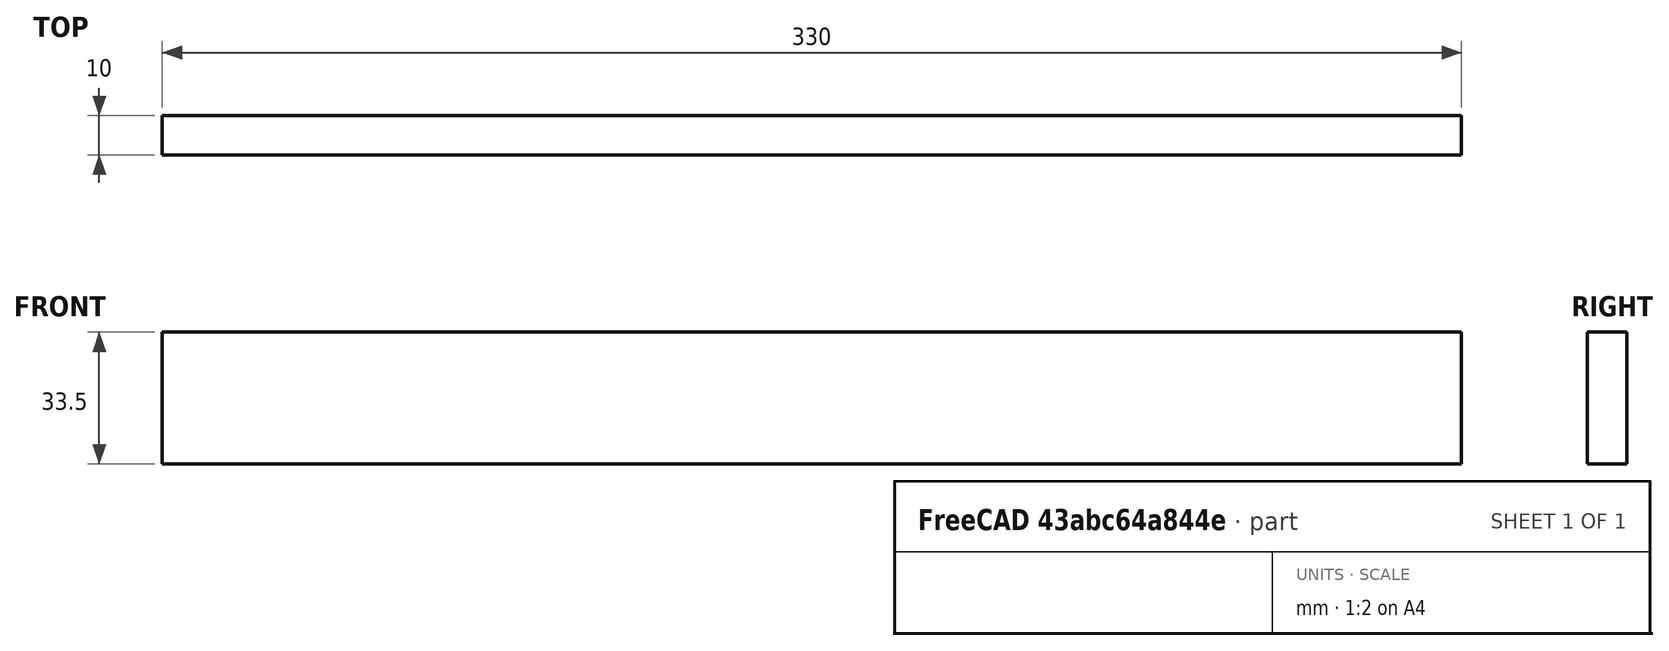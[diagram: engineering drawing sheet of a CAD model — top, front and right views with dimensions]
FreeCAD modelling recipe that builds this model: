
FCSTD DOCUMENT  (FreeCAD 0.18R16110 (Git))
Label: guide_330
License: All rights reserved
LicenseURL: http://en.wikipedia.org/wiki/All_rights_reserved
objects: App::Part×1, Sketcher::SketchObject×1, PartDesign::Pad×1, PartDesign::Body×1
note: 4 computed .brp shape members not serialized (recipe doc carries the construction recipe); baked Part::Feature solids carry a one-line shape summary decoded from their .brp

FEATURE [App::Part] Part
  Origin = -> Origin
FEATURE [Sketcher::SketchObject] Sketch
  MapMode = 5
  Support = -> [XY_Plane001]
  sketch-geometry (4):
    g0: LineSegment StartX=0 StartY=0 StartZ=0 EndX=330 EndY=0 EndZ=0
    g1: LineSegment StartX=330 StartY=0 StartZ=0 EndX=330 EndY=10 EndZ=0
    g2: LineSegment StartX=330 StartY=10 StartZ=0 EndX=0 EndY=10 EndZ=0
    g3: LineSegment StartX=0 StartY=10 StartZ=0 EndX=0 EndY=0 EndZ=0
  constraints (11):
    c: Coincident(g0,g1)
    c: Coincident(g1,g2)
    c: Coincident(g2,g3)
    c: Coincident(g3,g0)
    c: Horizontal(g0)
    c: Horizontal(g2)
    c: Vertical(g1)
    c: Vertical(g3)
    c: Coincident(g0,g-1)
    c: DistanceX(g0,g0) = 330
    c: DistanceY(g3,g3) = 10
FEATURE [PartDesign::Pad] Pad
  Length = 33.5
  Length2 = 100
  Profile = -> Sketch
  Type = 0
FEATURE [PartDesign::Body] Body
  Group = -> [Sketch,Pad]
  Origin = -> Origin001
  Tip = -> Pad
